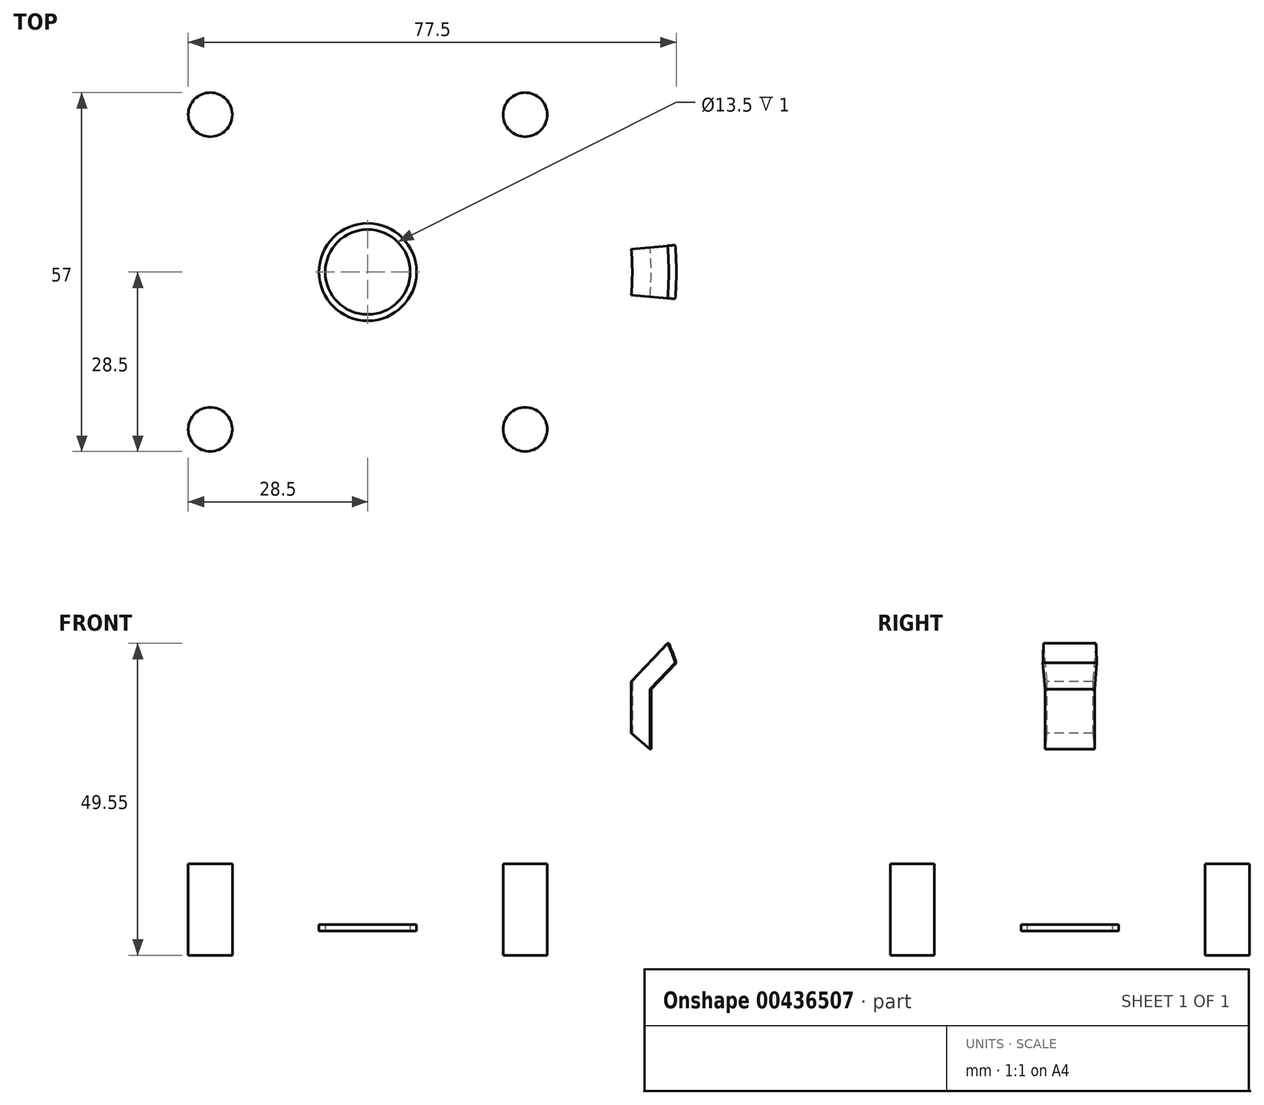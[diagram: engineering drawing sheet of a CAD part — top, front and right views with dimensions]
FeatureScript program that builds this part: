
annotation { "Feature Type Name" : "Feature", "Feature Type Description" : "" }
export const myFeature = defineFeature(function(context is Context, id is Id, definition is map)
    precondition{}
    {
        {
            var Q0;
            Q0=qCreatedBy(makeId("Front.planeOp"),FACE);
            var sketch = newSketch(context, id + "F0", { "sketchPlane" : qUnion([Q0])});
            skEllipticalArc(sketch, "E0", {});
            skPoint(sketch, "E1.end.orphan", {"position": v(7.75, 0.64) * mm});
            skPoint(sketch, "E2.center.orphan", {"position": v(0, 88.71) * mm});
            skFitSpline(sketch, "E3.0", {"points": [v(53.95, 30.83) * mm, v(54.02, 32.75) * mm, v(53.95, 34.67) * mm, v(53.66, 37.2) * mm, v(52.94, 40.31) * mm, v(51.55, 43.92) * mm, v(49.65, 47.36) * mm, v(47.27, 50.62) * mm, v(44.46, 53.68) * mm, v(41.77, 56.04) * mm, v(39.41, 57.82) * mm, v(37.55, 59.1) * mm, v(35.6, 60.3) * mm, v(32.9, 61.8) * mm, v(29.37, 63.5) * mm, v(24.89, 65.25) * mm, v(20.2, 66.69) * mm, v(15.34, 67.82) * mm, v(10.33, 68.64) * mm, v(6.07, 69.05) * mm, v(2.61, 69.22) * mm, v(0, 69.26) * mm, v(-2.61, 69.22) * mm, v(-6.07, 69.05) * mm, v(-10.33, 68.64) * mm, v(-15.34, 67.82) * mm, v(-20.2, 66.69) * mm, v(-24.89, 65.25) * mm, v(-29.37, 63.5) * mm, v(-32.9, 61.8) * mm, v(-35.6, 60.3) * mm, v(-37.55, 59.1) * mm, v(-39.41, 57.82) * mm, v(-41.77, 56.04) * mm, v(-44.46, 53.68) * mm, v(-47.27, 50.62) * mm, v(-49.65, 47.36) * mm, v(-51.55, 43.92) * mm, v(-52.94, 40.31) * mm, v(-53.66, 37.2) * mm, v(-53.95, 34.67) * mm, v(-54.02, 32.75) * mm, v(-53.95, 30.83) * mm, v(-53.66, 28.3) * mm, v(-52.94, 25.18) * mm, v(-51.55, 21.57) * mm, v(-49.65, 18.13) * mm, v(-47.27, 14.87) * mm, v(-44.46, 11.81) * mm, v(-41.77, 9.45) * mm, v(-39.41, 7.67) * mm, v(-37.55, 6.4) * mm, v(-35.6, 5.2) * mm, v(-32.9, 3.69) * mm, v(-29.37, 1.99) * mm, v(-24.89, 0.25) * mm, v(-20.2, -1.2) * mm, v(-15.34, -2.33) * mm, v(-10.33, -3.14) * mm, v(-6.07, -3.56) * mm, v(-2.61, -3.73) * mm, v(0, -3.77) * mm, v(2.61, -3.73) * mm, v(6.07, -3.56) * mm, v(10.33, -3.14) * mm, v(15.34, -2.33) * mm, v(20.2, -1.2) * mm, v(24.89, 0.25) * mm, v(29.37, 1.99) * mm, v(32.9, 3.69) * mm, v(35.6, 5.2) * mm, v(37.55, 6.4) * mm, v(39.41, 7.67) * mm, v(41.77, 9.45) * mm, v(44.46, 11.81) * mm, v(47.27, 14.87) * mm, v(49.65, 18.13) * mm, v(51.55, 21.57) * mm, v(52.94, 25.18) * mm, v(53.66, 28.3) * mm, v(53.95, 30.83) * mm, v(54.02, 32.75) * mm, v(53.95, 34.67) * mm]});
            skLineSegment(sketch, "E4", {"start": v(7.75, -3.38) * mm, "end": v(7.75, 0.64) * mm});
            skFitSpline(sketch, "E5", {"points": [v(53.95, 30.83) * mm, v(54.02, 32.75) * mm, v(53.95, 34.67) * mm, v(53.66, 37.2) * mm, v(52.94, 40.31) * mm, v(51.55, 43.92) * mm, v(49.65, 47.36) * mm, v(47.27, 50.62) * mm, v(44.46, 53.68) * mm, v(41.77, 56.04) * mm, v(39.41, 57.82) * mm, v(37.55, 59.1) * mm, v(35.6, 60.3) * mm, v(32.9, 61.8) * mm, v(29.37, 63.5) * mm, v(24.89, 65.25) * mm, v(20.2, 66.69) * mm, v(15.34, 67.82) * mm, v(10.33, 68.64) * mm, v(6.07, 69.05) * mm, v(2.61, 69.22) * mm, v(0, 69.26) * mm, v(-2.61, 69.22) * mm, v(-6.07, 69.05) * mm, v(-10.33, 68.64) * mm, v(-15.34, 67.82) * mm, v(-20.2, 66.69) * mm, v(-24.89, 65.25) * mm, v(-29.37, 63.5) * mm, v(-32.9, 61.8) * mm, v(-35.6, 60.3) * mm, v(-37.55, 59.1) * mm, v(-39.41, 57.82) * mm, v(-41.77, 56.04) * mm, v(-44.46, 53.68) * mm, v(-47.27, 50.62) * mm, v(-49.65, 47.36) * mm, v(-51.55, 43.92) * mm, v(-52.94, 40.31) * mm, v(-53.66, 37.2) * mm, v(-53.95, 34.67) * mm, v(-54.02, 32.75) * mm, v(-53.95, 30.83) * mm, v(-53.66, 28.3) * mm, v(-52.94, 25.18) * mm, v(-51.55, 21.57) * mm, v(-49.65, 18.13) * mm, v(-47.27, 14.87) * mm, v(-44.46, 11.81) * mm, v(-41.77, 9.45) * mm, v(-39.41, 7.67) * mm, v(-37.55, 6.4) * mm, v(-35.6, 5.2) * mm, v(-32.9, 3.69) * mm, v(-29.37, 1.99) * mm, v(-24.89, 0.25) * mm, v(-20.2, -1.2) * mm, v(-15.34, -2.33) * mm, v(-10.33, -3.14) * mm, v(-6.07, -3.56) * mm, v(-2.61, -3.73) * mm, v(0, -3.77) * mm, v(2.61, -3.73) * mm, v(6.07, -3.56) * mm, v(10.33, -3.14) * mm, v(15.34, -2.33) * mm, v(20.2, -1.2) * mm, v(24.89, 0.25) * mm, v(29.37, 1.99) * mm, v(32.9, 3.69) * mm, v(35.6, 5.2) * mm, v(37.55, 6.4) * mm, v(39.41, 7.67) * mm, v(41.77, 9.45) * mm, v(44.46, 11.81) * mm, v(47.27, 14.87) * mm, v(49.65, 18.13) * mm, v(51.55, 21.57) * mm, v(52.94, 25.18) * mm, v(53.66, 28.3) * mm, v(53.95, 30.83) * mm, v(54.02, 32.75) * mm, v(53.95, 34.67) * mm, v(53.95, 30.83) * mm]});
            skLineSegment(sketch, "E6", {"start": v(0, 0) * mm, "end": v(0, 75.18) * mm});
            skLineSegment(sketch, "E7", {"start": v(7.75, -3.38) * mm, "end": v(6.75, -3.38) * mm});
            skLineSegment(sketch, "E8", {"start": v(6.75, -3.38) * mm, "end": v(6.75, -2.38) * mm});
            skLineSegment(sketch, "E9", {"start": v(6.75, -2.38) * mm, "end": v(7.75, -2.38) * mm});
            skEllipticalArc(sketch, "E10", {});
            skFitSpline(sketch, "E11", {"points": [v(53.94, 93.63) * mm, v(54.02, 95.56) * mm, v(53.96, 97.49) * mm, v(53.68, 100.03) * mm, v(52.97, 103.17) * mm, v(51.59, 106.8) * mm, v(49.7, 110.27) * mm, v(47.33, 113.56) * mm, v(44.52, 116.64) * mm, v(41.83, 119.03) * mm, v(39.47, 120.83) * mm, v(37.6, 122.12) * mm, v(35.65, 123.34) * mm, v(32.95, 124.87) * mm, v(29.41, 126.6) * mm, v(24.92, 128.36) * mm, v(20.22, 129.83) * mm, v(15.34, 131) * mm, v(10.32, 131.84) * mm, v(6.03, 132.28) * mm, v(2.56, 132.46) * mm, v(-0.06, 132.52) * mm, v(-2.68, 132.5) * mm, v(-6.15, 132.34) * mm, v(-10.44, 131.94) * mm, v(-15.48, 131.15) * mm, v(-20.36, 130.03) * mm, v(-25.08, 128.61) * mm, v(-29.59, 126.88) * mm, v(-33.15, 125.2) * mm, v(-35.86, 123.7) * mm, v(-37.83, 122.5) * mm, v(-39.7, 121.22) * mm, v(-42.08, 119.45) * mm, v(-44.8, 117.08) * mm, v(-47.64, 114.03) * mm, v(-50.03, 110.76) * mm, v(-51.96, 107.31) * mm, v(-53.38, 103.7) * mm, v(-54.12, 100.57) * mm, v(-54.42, 98.02) * mm, v(-54.5, 96.1) * mm, v(-54.44, 94.17) * mm, v(-54.16, 91.62) * mm, v(-53.46, 88.48) * mm, v(-52.07, 84.85) * mm, v(-50.18, 81.38) * mm, v(-47.81, 78.1) * mm, v(-45, 75) * mm, v(-42.3, 72.62) * mm, v(-39.95, 70.82) * mm, v(-38.09, 69.53) * mm, v(-36.13, 68.31) * mm, v(-33.44, 66.78) * mm, v(-29.9, 65.06) * mm, v(-25.4, 63.29) * mm, v(-20.7, 61.82) * mm, v(-15.82, 60.66) * mm, v(-10.8, 59.81) * mm, v(-6.52, 59.37) * mm, v(-3.05, 59.19) * mm, v(-0.42, 59.13) * mm, v(2.2, 59.16) * mm, v(5.67, 59.31) * mm, v(9.96, 59.7) * mm, v(15, 60.5) * mm, v(19.88, 61.62) * mm, v(24.6, 63.04) * mm, v(29.1, 64.77) * mm, v(32.66, 66.46) * mm, v(35.38, 67.96) * mm, v(37.34, 69.16) * mm, v(39.22, 70.43) * mm, v(41.6, 72.2) * mm, v(44.31, 74.57) * mm, v(47.15, 77.62) * mm, v(49.55, 80.89) * mm, v(51.48, 84.34) * mm, v(52.9, 87.96) * mm, v(53.64, 91.08) * mm, v(53.94, 93.63) * mm, v(54.02, 95.56) * mm, v(53.96, 97.49) * mm]});
            skLineSegment(sketch, "E12", {"start": v(22.5, 66.66) * mm, "end": v(25, 63.24) * mm});
            skPoint(sketch, "E13.center.orphan", {"position": v(0, 95.68) * mm});
            skLineSegment(sketch, "E14", {"start": v(49, 39.21) * mm, "end": v(45, 35) * mm});
            skLineSegment(sketch, "E15", {"start": v(45, 35) * mm, "end": v(45, 25.5) * mm});
            skLineSegment(sketch, "E16.0", {"start": v(42, 36.2) * mm, "end": v(42, 28) * mm});
            skLineSegment(sketch, "E16.1", {"start": v(47.8, 42.3) * mm, "end": v(42, 36.2) * mm});
            skLineSegment(sketch, "E17", {"start": v(42, 28) * mm, "end": v(45, 25.5) * mm});
            skFitSpline(sketch, "E18", {"points": [v(53.95, 30.83) * mm, v(54.02, 32.75) * mm, v(53.95, 34.67) * mm, v(53.66, 37.2) * mm, v(52.94, 40.31) * mm, v(51.55, 43.92) * mm, v(49.65, 47.36) * mm, v(47.27, 50.62) * mm, v(44.46, 53.68) * mm, v(41.77, 56.04) * mm, v(39.41, 57.82) * mm, v(37.55, 59.1) * mm, v(35.6, 60.3) * mm, v(32.9, 61.8) * mm, v(29.37, 63.5) * mm, v(24.89, 65.25) * mm, v(20.2, 66.69) * mm, v(15.34, 67.82) * mm, v(10.33, 68.64) * mm, v(6.07, 69.05) * mm, v(2.61, 69.22) * mm, v(0, 69.26) * mm, v(-2.61, 69.22) * mm, v(-6.07, 69.05) * mm, v(-10.33, 68.64) * mm, v(-15.34, 67.82) * mm, v(-20.2, 66.69) * mm, v(-24.89, 65.25) * mm, v(-29.37, 63.5) * mm, v(-32.9, 61.8) * mm, v(-35.6, 60.3) * mm, v(-37.55, 59.1) * mm, v(-39.41, 57.82) * mm, v(-41.77, 56.04) * mm, v(-44.46, 53.68) * mm, v(-47.27, 50.62) * mm, v(-49.65, 47.36) * mm, v(-51.55, 43.92) * mm, v(-52.94, 40.31) * mm, v(-53.66, 37.2) * mm, v(-53.95, 34.67) * mm, v(-54.02, 32.75) * mm, v(-53.95, 30.83) * mm, v(-53.66, 28.3) * mm, v(-52.94, 25.18) * mm, v(-51.55, 21.57) * mm, v(-49.65, 18.13) * mm, v(-47.27, 14.87) * mm, v(-44.46, 11.81) * mm, v(-41.77, 9.45) * mm, v(-39.41, 7.67) * mm, v(-37.55, 6.4) * mm, v(-35.6, 5.2) * mm, v(-32.9, 3.69) * mm, v(-29.37, 1.99) * mm, v(-24.89, 0.25) * mm, v(-20.2, -1.2) * mm, v(-15.34, -2.33) * mm, v(-10.33, -3.14) * mm, v(-6.07, -3.56) * mm, v(-2.61, -3.73) * mm, v(0, -3.77) * mm, v(2.61, -3.73) * mm, v(6.07, -3.56) * mm, v(10.33, -3.14) * mm, v(15.34, -2.33) * mm, v(20.2, -1.2) * mm, v(24.89, 0.25) * mm, v(29.37, 1.99) * mm, v(32.9, 3.69) * mm, v(35.6, 5.2) * mm, v(37.55, 6.4) * mm, v(39.41, 7.67) * mm, v(41.77, 9.45) * mm, v(44.46, 11.81) * mm, v(47.27, 14.87) * mm, v(49.65, 18.13) * mm, v(51.55, 21.57) * mm, v(52.94, 25.18) * mm, v(53.66, 28.3) * mm, v(53.95, 30.83) * mm, v(54.02, 32.75) * mm, v(53.95, 34.67) * mm]});
            skLineSegment(sketch, "E19.bottom", {"start": v(49.27, 33.7) * mm, "end": v(55.5, 33.7) * mm});
            skLineSegment(sketch, "E19.top", {"start": v(49.27, 31.3) * mm, "end": v(55.5, 31.3) * mm});
            skLineSegment(sketch, "E19.left", {"start": v(49.27, 33.7) * mm, "end": v(49.27, 31.3) * mm});
            skLineSegment(sketch, "E19.right", {"start": v(55.5, 33.7) * mm, "end": v(55.5, 31.3) * mm});
            const initialGuessF0  = {"E0": [0, 0.03274645100706606, 1, 0, 0.05, 0.0325, 4.868016433728875, 1.3181160716528195], "E10": [-0.00024172439614509168, 0.09582555252217098, 0.9999877386341905, -0.004952027996484204, 0.05020448508790766, 0.03264330102065433, 4.972214005821244, 5.185719723849428]};
            skSetInitialGuess(sketch, initialGuessF0);
            skSolve(sketch);
        }
        {
            var Q0;
            {var subQ0=sQuery(id+"F0.wireOp",EDGE,"E14");Q0=makeQuery(id+"F0.imprint","IMPRINT",FACE,{"disambiguationData":[TD([[makeQuery(id+"F0.imprint","IMPRINT",EDGE,{"derivedFrom":subQ0}),-1.0]])]});}
            var Q1;
            Q1=sQuery(id+"F0.wireOp",EDGE,"E6");
            revolve(context, id + "F1", {"entities" : qUnion([Q0]), "axis" : qUnion([Q1]), "revolveType" : RevolveType.SYMMETRIC, "angle" : 10 * degree});
        }
        {
            var Q0;
            {var subQ0=sQuery(id+"F0.wireOp",EDGE,"E3.0");Q0=makeQuery(id+"F0.imprint","IMPRINT",FACE,{"disambiguationData":[TD([[makeQuery(id+"F0.imprint","IMPRINT",EDGE,{"derivedFrom":subQ0}),1.0]])]});}
            var Q1;
            {var subQ0=sQuery(id+"F0.wireOp",EDGE,"E10");Q1=makeQuery(id+"F0.imprint","IMPRINT",FACE,{"disambiguationData":[TD([[makeQuery(id+"F0.imprint","IMPRINT",EDGE,{"derivedFrom":subQ0}),-1.0]])]});}
            var Q2;
            {var subQ0=sQuery(id+"F0.wireOp",EDGE,"E7");Q2=makeQuery(id+"F0.imprint","IMPRINT",FACE,{"disambiguationData":[TD([[makeQuery(id+"F0.imprint","IMPRINT",EDGE,{"derivedFrom":subQ0}),-1.0]])]});}
            var Q3;
            Q3=sQuery(id+"F0.wireOp",EDGE,"E6");
            revolve(context, id + "F2", {"operationType" : NewBodyOperationType.ADD, "entities" : qUnion([Q0, Q1, Q2]), "axis" : qUnion([Q3]), "revolveType" : RevolveType.FULL});
        }
        {
            var Q0;
            {var subQ5=sQuery(id+"F0.wireOp",EDGE,"E19.left");Q0=makeQuery(id+"F0.imprint","IMPRINT",FACE,{"disambiguationData":[TD([[makeQuery(id+"F0.imprint","IMPRINT",EDGE,{"derivedFrom":subQ5}),1.0]])]});}
            var Q1;
            {var subQ0=sQuery(id+"F0.wireOp",EDGE,"E19.bottom");var subQ1=sQuery(id+"F0.wireOp",EDGE,"E0");var subQ2=makeQuery(id+"F0.imprint","INTERSECT",VERTEX,{"derivedFrom":[subQ1,subQ0]});Q1=makeQuery(id+"F0.imprint","IMPRINT",FACE,{"disambiguationData":[TD([[makeQuery(id+"F0.imprint","IMPRINT",EDGE,{"disambiguationData":[TD([[subQ2,1.0]])],"derivedFrom":subQ1}),-1.0]])]});}
            var Q2;
            {var subQ0=sQuery(id+"F0.wireOp",EDGE,"E19.right");Q2=makeQuery(id+"F0.imprint","IMPRINT",FACE,{"disambiguationData":[TD([[makeQuery(id+"F0.imprint","IMPRINT",EDGE,{"derivedFrom":subQ0}),-1.0]])]});}
            extrude(context, id + "F3", {"entities" : qUnion([Q0, Q1, Q2]), "endBound" : BoundingType.SYMMETRIC, "depth" : 2 * mm});
        }
        {
            var Q0;
            Q0=makeQuery(id+"F3.opExtrude","SWEPT_BODY",BODY,{"disambiguationData":[OSD([sQuery(id+"F0.wireOp",EDGE,"E19.bottom"),sQuery(id+"F0.wireOp",EDGE,"E19.top"),sQuery(id+"F0.wireOp",EDGE,"E19.left"),sQuery(id+"F0.wireOp",EDGE,"E19.right")])]});
            var Q1;
            Q1=makeQuery(id+"F1.opRevolve","SWEPT_BODY",BODY,{"disambiguationData":[OSD([sQuery(id+"F0.wireOp",EDGE,"E0"),sQuery(id+"F0.wireOp",EDGE,"E14"),sQuery(id+"F0.wireOp",EDGE,"E15"),sQuery(id+"F0.wireOp",EDGE,"E16.0"),sQuery(id+"F0.wireOp",EDGE,"E16.1"),sQuery(id+"F0.wireOp",EDGE,"E17")])]});
            booleanBodies(context, id + "F4", {"operationType" : BooleanOperationType.SUBTRACTION, "tools" : qUnion([Q0]), "targets" : qUnion([Q1])});
        }
        {
            var Q0;
            Q0=qCreatedBy(makeId("Top.planeOp"),FACE);
            var sketch = newSketch(context, id + "F5", { "sketchPlane" : qUnion([Q0])});
            skCircle(sketch, "E20", {"center": v(-25, -25) * mm, "radius": 3.5 * mm});
            skCircle(sketch, "E21", {"center": v(25, -25) * mm, "radius": 3.5 * mm});
            skCircle(sketch, "E22", {"center": v(25, 25) * mm, "radius": 3.5 * mm});
            skCircle(sketch, "E23", {"center": v(-25, 25) * mm, "radius": 3.5 * mm});
            skSolve(sketch);
        }
        {
            var Q0;
            Q0 = qSketchRegion(id + "F5", true);
            extrude(context, id + "F6", {"entities" : qUnion([Q0]), "operationType" : NewBodyOperationType.ADD, "endBound" : BoundingType.SYMMETRIC, "depth" : 14.5 * mm});
        }
    });
